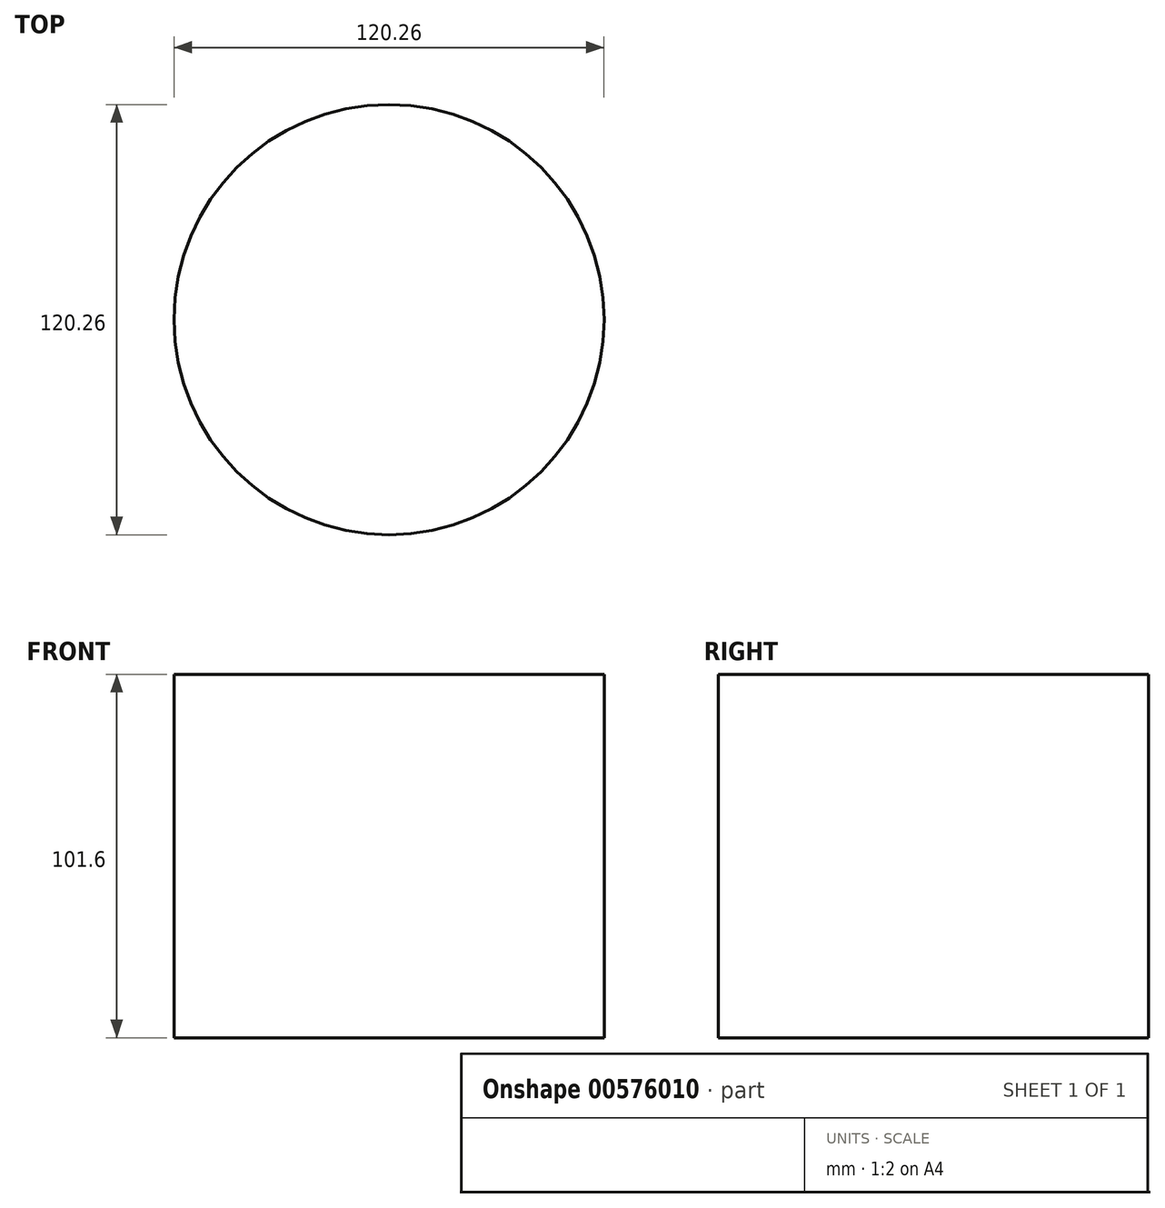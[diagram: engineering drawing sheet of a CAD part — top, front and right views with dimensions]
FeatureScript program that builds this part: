
annotation { "Feature Type Name" : "Feature", "Feature Type Description" : "" }
export const myFeature = defineFeature(function(context is Context, id is Id, definition is map)
    precondition{}
    {
        {
            var Q0;
            Q0=qCreatedBy(makeId("Front.planeOp"),FACE);
            var sketch = newSketch(context, id + "F0", { "sketchPlane" : qUnion([Q0])});
            skLineSegment(sketch, "E0", {"start": v(0, 0) * mm, "end": v(60.13, 0) * mm});
            skLineSegment(sketch, "E1", {"start": v(60.13, 0) * mm, "end": v(60.13, -101.6) * mm});
            skLineSegment(sketch, "E2", {"start": v(60.13, -101.6) * mm, "end": v(9.33, -101.6) * mm});
            skLineSegment(sketch, "E3", {"start": v(9.33, -101.6) * mm, "end": v(0, -101.6) * mm});
            skLineSegment(sketch, "E4", {"start": v(0, -101.6) * mm, "end": v(0, 0) * mm});
            skSolve(sketch);
        }
        {
            var Q0;
            Q0=makeQuery(id+"F0.imprint","IMPRINT",FACE,{"disambiguationData":[TD([[makeQuery(id+"F0.imprint","IMPRINT",EDGE,{"derivedFrom":sQuery(id+"F0.wireOp",EDGE,"E0")}),-1.0]])]});
            var Q1;
            Q1=sQuery(id+"F0.wireOp",EDGE,"E4");
            revolve(context, id + "F1", {"entities" : qUnion([Q0]), "axis" : qUnion([Q1]), "revolveType" : RevolveType.FULL});
        }
    });
